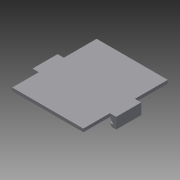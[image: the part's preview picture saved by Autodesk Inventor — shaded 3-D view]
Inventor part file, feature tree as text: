
AUTODESK INVENTOR PART (.ipt)
format: ipt  version: 2013 (Build 170138000, 138)  size: 129,536 bytes
history: native  units: mm
features: extrude x6, sketch x6
ambient origin geometry x8: Origin, YZ Plane, XZ Plane, XY Plane, X Axis, Y Axis, Z Axis, Center Point
bodies: Solid1 (feature_tree)
feature tree (12):
  extrude  "Extrusion1"  Depth=54.0mm
  extrude  "Extrusion2"  Depth=14.0mm
  extrude  "Extrusion3"  Depth=4.0mm
  extrude  "Extrusion4"  Depth=21.0mm
  extrude  "Extrusion5"  Depth=4.0mm
  extrude  "Extrusion6"  Depth=21.0mm
  sketch  "Sketch1"  dims[d0=45.5mm d1=54.0mm]
  sketch  "Sketch2"  dims[d2=4.0mm d3=14.0mm]
  sketch  "Sketch3"  dims[d4=21.0mm d5=4.0mm]
  sketch  "Sketch4"  dims[d6=14.0mm d7=21.0mm]
  sketch  "Sketch5"  dims[d8=2.0mm d9=0.0mm d10=4.0mm]
  sketch  "Sketch6"  dims[d11=16.0mm d12=21.0mm d13=4.0mm d14=7.0mm d15=0.0mm d16=1.8mm d17=2.1mm d18=24.75mm d19=0.0mm d20=1.8mm d21=2.1mm d22=176.5mm d23=0.0mm d24=3535.5mm d25=0.0mm d26=5309.5mm d27=0.0mm]
